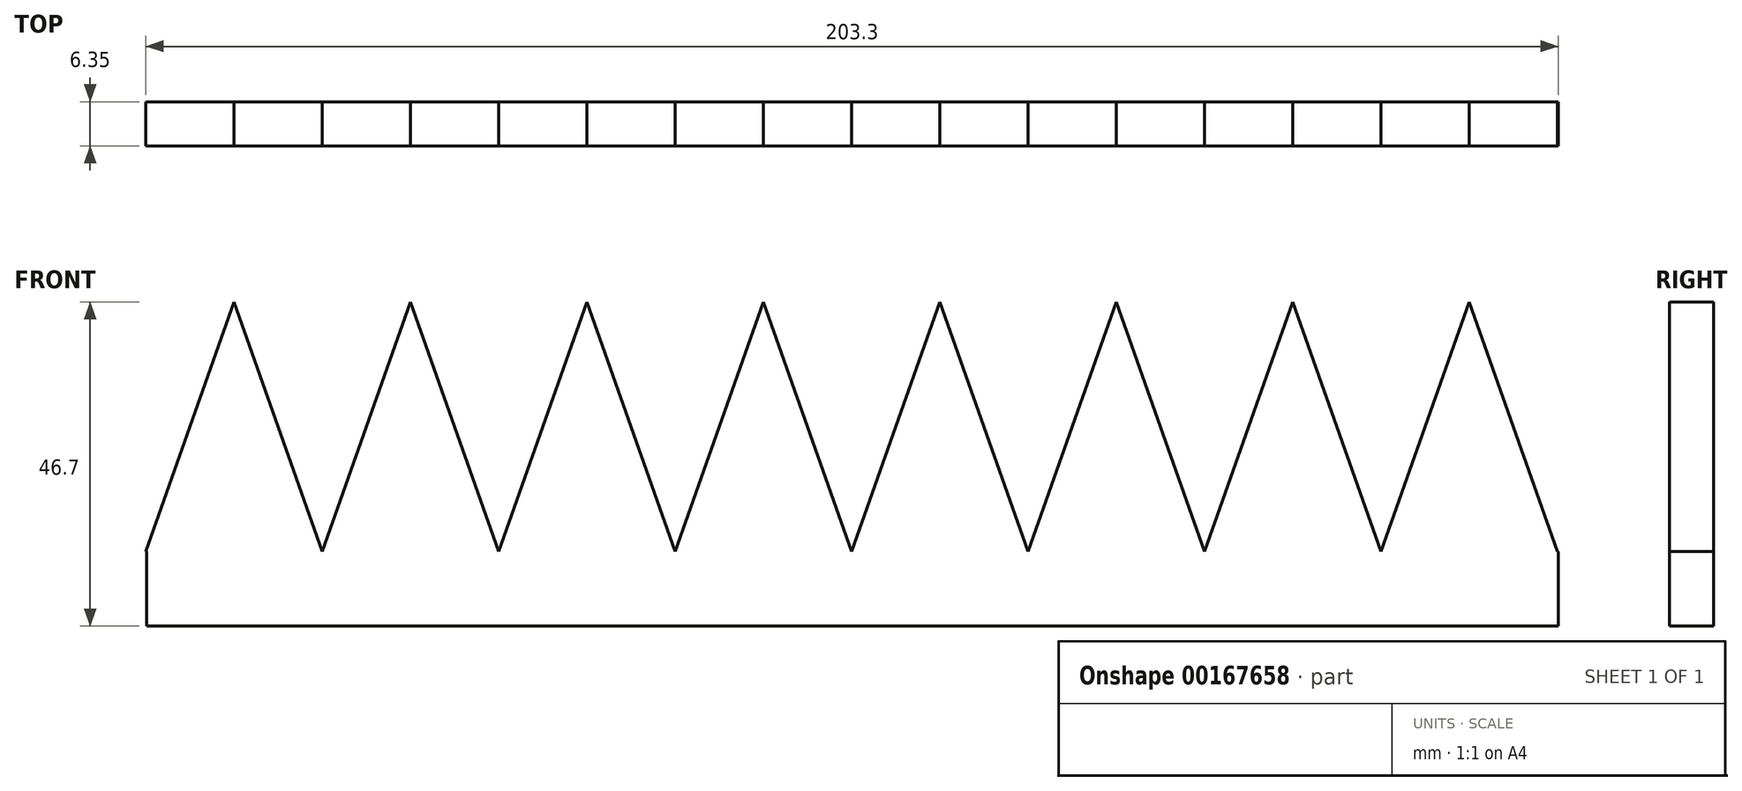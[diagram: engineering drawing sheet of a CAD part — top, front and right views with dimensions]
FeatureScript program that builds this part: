
annotation { "Feature Type Name" : "Feature", "Feature Type Description" : "" }
export const myFeature = defineFeature(function(context is Context, id is Id, definition is map)
    precondition{}
    {
        {
            var Q0;
            Q0=qCreatedBy(makeId("Front.planeOp"),FACE);
            var sketch = newSketch(context, id + "F0", { "sketchPlane" : qUnion([Q0])});
            skLineSegment(sketch, "E0.bottom", {"start": v(-101.6, 5.39) * mm, "end": v(101.6, 5.39) * mm});
            skLineSegment(sketch, "E0.top", {"start": v(-101.6, -5.39) * mm, "end": v(101.6, -5.39) * mm});
            skLineSegment(sketch, "E0.left", {"start": v(-101.6, 5.39) * mm, "end": v(-101.6, -5.39) * mm});
            skLineSegment(sketch, "E0.right", {"start": v(101.6, 5.39) * mm, "end": v(101.6, -5.39) * mm});
            skPoint(sketch, "E0.middle", {"position": v(0, 0) * mm});
            skLineSegment(sketch, "E1.0", {"start": v(-76.3, 5.39) * mm, "end": v(-101.7, 5.39) * mm});
            skLineSegment(sketch, "E1.1", {"start": v(-101.7, 5.39) * mm, "end": v(-89, 41.3) * mm});
            skLineSegment(sketch, "E1.2", {"start": v(-89, 41.3) * mm, "end": v(-76.3, 5.39) * mm});
            skPoint(sketch, "E1.0.midPoint", {"position": v(-89, 5.39) * mm});
            skLineSegment(sketch, "E2.1.0.0", {"start": v(-76.3, 5.39) * mm, "end": v(-63.6, 41.3) * mm});
            skLineSegment(sketch, "E2.1.0.1", {"start": v(-63.6, 41.3) * mm, "end": v(-50.9, 5.39) * mm});
            skLineSegment(sketch, "E2.1.0.2", {"start": v(-50.9, 5.39) * mm, "end": v(-76.3, 5.39) * mm});
            skLineSegment(sketch, "E2.2.0.0", {"start": v(-50.9, 5.39) * mm, "end": v(-38.2, 41.3) * mm});
            skLineSegment(sketch, "E2.2.0.1", {"start": v(-38.2, 41.3) * mm, "end": v(-25.5, 5.39) * mm});
            skLineSegment(sketch, "E2.2.0.2", {"start": v(-25.5, 5.39) * mm, "end": v(-50.9, 5.39) * mm});
            skLineSegment(sketch, "E2.direction1", {"start": v(-101.7, 5.39) * mm, "end": v(-76.3, 5.39) * mm, "construction": true});
            skLineSegment(sketch, "E3.0.3.0", {"start": v(-25.5, 5.39) * mm, "end": v(-12.8, 41.3) * mm});
            skLineSegment(sketch, "E3.3.3.0", {"start": v(-12.8, 41.3) * mm, "end": v(-0.1, 5.39) * mm});
            skLineSegment(sketch, "E3.6.3.0", {"start": v(-0.1, 5.39) * mm, "end": v(-25.5, 5.39) * mm});
            skLineSegment(sketch, "E4.0.4.0", {"start": v(-0.1, 5.39) * mm, "end": v(12.6, 41.3) * mm});
            skLineSegment(sketch, "E4.3.4.0", {"start": v(12.6, 41.3) * mm, "end": v(25.3, 5.39) * mm});
            skLineSegment(sketch, "E4.6.4.0", {"start": v(25.3, 5.39) * mm, "end": v(-0.1, 5.39) * mm});
            skLineSegment(sketch, "E4.0.5.0", {"start": v(25.3, 5.39) * mm, "end": v(38, 41.3) * mm});
            skLineSegment(sketch, "E4.3.5.0", {"start": v(38, 41.3) * mm, "end": v(50.7, 5.39) * mm});
            skLineSegment(sketch, "E4.6.5.0", {"start": v(50.7, 5.39) * mm, "end": v(25.3, 5.39) * mm});
            skLineSegment(sketch, "E4.0.6.0", {"start": v(50.7, 5.39) * mm, "end": v(63.4, 41.3) * mm});
            skLineSegment(sketch, "E4.3.6.0", {"start": v(63.4, 41.3) * mm, "end": v(76.1, 5.39) * mm});
            skLineSegment(sketch, "E4.6.6.0", {"start": v(76.1, 5.39) * mm, "end": v(50.7, 5.39) * mm});
            skLineSegment(sketch, "E4.0.7.0", {"start": v(76.1, 5.39) * mm, "end": v(88.8, 41.3) * mm});
            skLineSegment(sketch, "E4.3.7.0", {"start": v(88.8, 41.3) * mm, "end": v(101.5, 5.39) * mm});
            skLineSegment(sketch, "E4.6.7.0", {"start": v(101.5, 5.39) * mm, "end": v(76.1, 5.39) * mm});
            skSolve(sketch);
        }
        {
            var Q0;
            Q0 = qSketchRegion(id + "F0", true);
            extrude(context, id + "F1", {"entities" : qUnion([Q0]), "depth" : 6.35 * mm});
        }
    });
